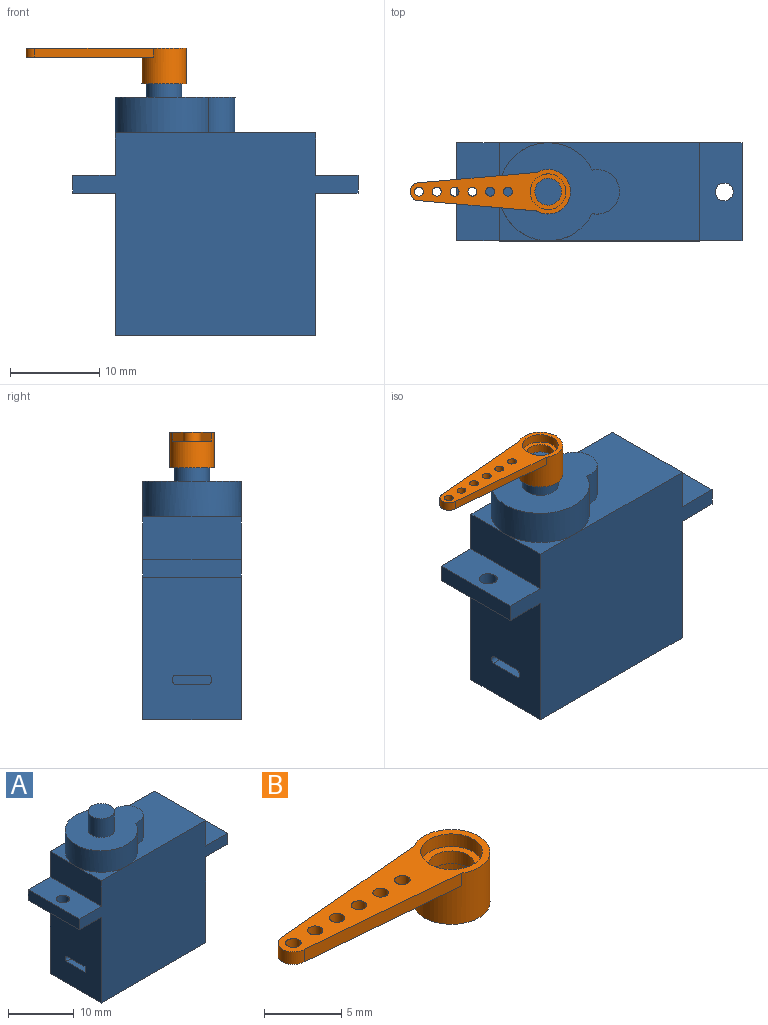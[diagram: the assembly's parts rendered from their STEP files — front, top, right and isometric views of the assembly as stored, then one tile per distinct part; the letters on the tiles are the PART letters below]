
ASSEMBLY  parts=2 mates=1
PART A: 28 faces, bbox 32x11x30.3 mm
  f0: plane 16x11mm, normal (-1,0,0), area 171.7mm2, adj f4,f6,f8,f13,f23,f24,f25,f26
  f1: plane 17x11mm, normal (0,0,1), area 128.7mm2, adj f4,f6,f7,f18,f19
  f2: plane 5.5x5.5mm, normal (0,0,1), area 6.5mm2, adj f4,f5,f18
  f3: plane 16x11mm, normal (1,0,0), area 176mm2, adj f4,f6,f8,f17
  f4: plane 32x22.75mm, normal (0,1,0), area 530.9mm2, adj f0,f1,f2,f3,f5,f7,f8,f10
  f5: plane 11x4.75mm, normal (-1,0,0), area 52.3mm2, adj f2,f4,f6,f9,f12
  f6: plane 32x22.75mm, normal (0,-1,0), area 530.9mm2, adj f0,f1,f3,f5,f7,f8,f9,f10
  f7: plane 11x4.75mm, normal (1,0,0), area 52.3mm2, adj f1,f4,f6,f16
  f8: plane 22.5x11mm, normal (0,0,-1), area 247.5mm2, adj f0,f3,f4,f6
  f9: plane 5.5x5.5mm, normal (0,0,1), area 6.5mm2, adj f5,f6,f18
  f10: plane 11x2mm, normal (-1,0,0), area 22mm2, adj f4,f6,f12,f13
  f11: cylinder r=1mm len=2mm, axis (0,0,-1), area 12.6mm2, adj f12,f13
  f12: plane 11x4.75mm, normal (0,0,1), area 49.1mm2, adj f4,f5,f6,f10,f11
  f13: plane 11x4.75mm, normal (0,0,-1), area 49.1mm2, adj f0,f4,f6,f10,f11
  f14: plane 11x2mm, normal (1,0,0), area 22mm2, adj f4,f6,f16,f17
  f15: cylinder r=1mm len=2mm, axis (0,0,-1), area 12.6mm2, adj f16,f17
  f16: plane 11x4.75mm, normal (0,0,1), area 49.1mm2, adj f4,f6,f7,f14,f15
  f17: plane 11x4.75mm, normal (0,0,-1), area 49.1mm2, adj f3,f4,f6,f14,f15
  f18: cylinder r=5.5mm len=11mm, axis (0,0,-1), area 118.1mm2, adj f1,f2,f9,f19,f20
  f19: cylinder r=2.5mm len=5mm, axis (0,0,-1), area 36mm2, adj f1,f18,f20
  f20: plane 13.5x11mm, normal (0,0,1), area 93.2mm2, adj f18,f19,f21
  f21: cylinder r=2mm len=4mm, axis (0,0,-1), area 44mm2, adj f20,f22
  f22: plane 4x4mm, normal (0,0,1), area 12.6mm2, adj f21
  f23: plane 4x2mm, normal (0,0,-1), area 8mm2, adj f0,f24,f26,f27
  f24: cylinder r=0.7mm len=2mm, axis (-1,0,0), area 2.2mm2, adj f0,f23,f25,f27
  f25: plane 4x2mm, normal (0,0,1), area 8mm2, adj f0,f24,f26,f27
  f26: cylinder r=0.7mm len=2mm, axis (-1,0,0), area 2.2mm2, adj f0,f23,f25,f27
  f27: plane 4.42x1mm, normal (-1,0,0), area 4.3mm2, adj f23,f24,f25,f26
PART B: 18 faces, bbox 18x5x4 mm
  f0: cylinder r=2mm len=4mm, axis (0,0,-1), area 25.1mm2, adj f2,f3
  f1: cylinder r=2.5mm len=5mm, axis (0,0,-1), area 57.6mm2, adj f2,f7,f8,f15,f17
  f2: plane 5x5mm, normal (0,0,-1), area 7.1mm2, adj f0,f1
  f3: plane 4x4mm, normal (0,0,-1), area 5.5mm2, adj f0,f4
  f4: cylinder r=1.5mm len=3mm, axis (0,0,-1), area 9.4mm2, adj f3,f5
  f5: plane 4x4mm, normal (0,0,1), area 5.5mm2, adj f4,f6
  f6: cylinder r=2mm len=4mm, axis (0,0,-1), area 12.6mm2, adj f5,f17
  f7: plane 14.26x4.34mm, normal (0,0,-1), area 35mm2, adj f1,f8,f9,f10,f11,f12,f13,f14
  f8: plane 13.26x1.17mm, normal (-0.09,1,0), area 13.3mm2, adj f1,f7,f9,f17
  f9: cylinder r=1mm len=2mm, axis (0,0,-1), area 3.1mm2, adj f7,f8,f15,f17
  f10: cylinder r=0.5mm len=1mm, axis (0,0,-1), area 3.1mm2, adj f7,f17
  f11: cylinder r=0.5mm len=1mm, axis (0,0,-1), area 3.1mm2, adj f7,f17
  f12: cylinder r=0.5mm len=1mm, axis (0,0,-1), area 3.1mm2, adj f7,f17
  f13: cylinder r=0.5mm len=1mm, axis (0,0,-1), area 3.1mm2, adj f7,f17
  f14: cylinder r=0.5mm len=1mm, axis (0,0,-1), area 3.1mm2, adj f7,f17
  f15: plane 13.26x1.17mm, normal (-0.09,-1,0), area 13.3mm2, adj f1,f7,f9,f17
  f16: cylinder r=0.5mm len=1mm, axis (0,0,-1), area 3.1mm2, adj f7,f17
  f17: plane 18x5mm, normal (0,0,1), area 42.1mm2, adj f1,f6,f8,f9,f10,f11,f12,f13
PLACE A t=(-11.5,-7.65,-23.03)mm
PLACE B t=(-17.25,-7.65,5.22)mm
MATE revolute B.f0 <-> A.f21  axis (0,0,-1) through (-17.25,-7.65,7.22)mm
